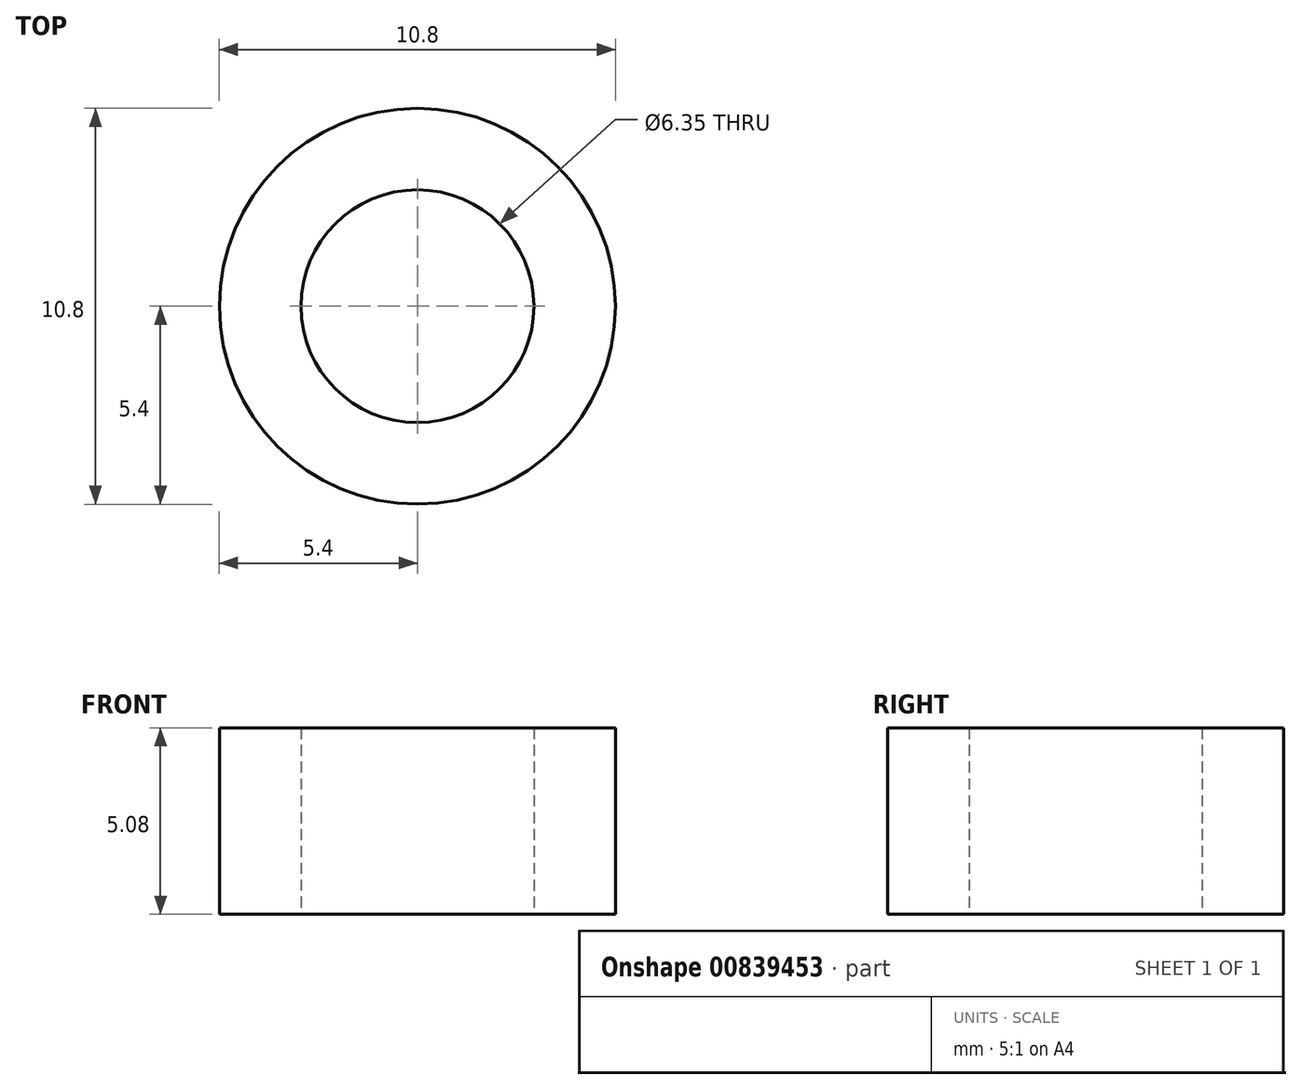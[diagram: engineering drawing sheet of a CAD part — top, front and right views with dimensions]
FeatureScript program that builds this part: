
annotation { "Feature Type Name" : "Feature", "Feature Type Description" : "" }
export const myFeature = defineFeature(function(context is Context, id is Id, definition is map)
    precondition{}
    {
        {
            var Q0;
            Q0=qCreatedBy(makeId("Top.planeOp"),FACE);
            var sketch = newSketch(context, id + "F0", { "sketchPlane" : qUnion([Q0])});
            skCircle(sketch, "E0", {"center": v(0, 0) * mm, "radius": 3.18 * mm});
            skCircle(sketch, "E1", {"center": v(0, 0) * mm, "radius": 5.4 * mm});
            skSolve(sketch);
        }
        {
            var Q0;
            Q0=makeQuery(id+"F0.imprint","IMPRINT",FACE,{"disambiguationData":[TD([[makeQuery(id+"F0.imprint","IMPRINT",EDGE,{"derivedFrom":sQuery(id+"F0.wireOp",EDGE,"E0")}),-1.0]])]});
            extrude(context, id + "F1", {"entities" : qUnion([Q0]), "depth" : 5.08 * mm, "offsetDistance" : 25.4 * mm});
        }
    });
